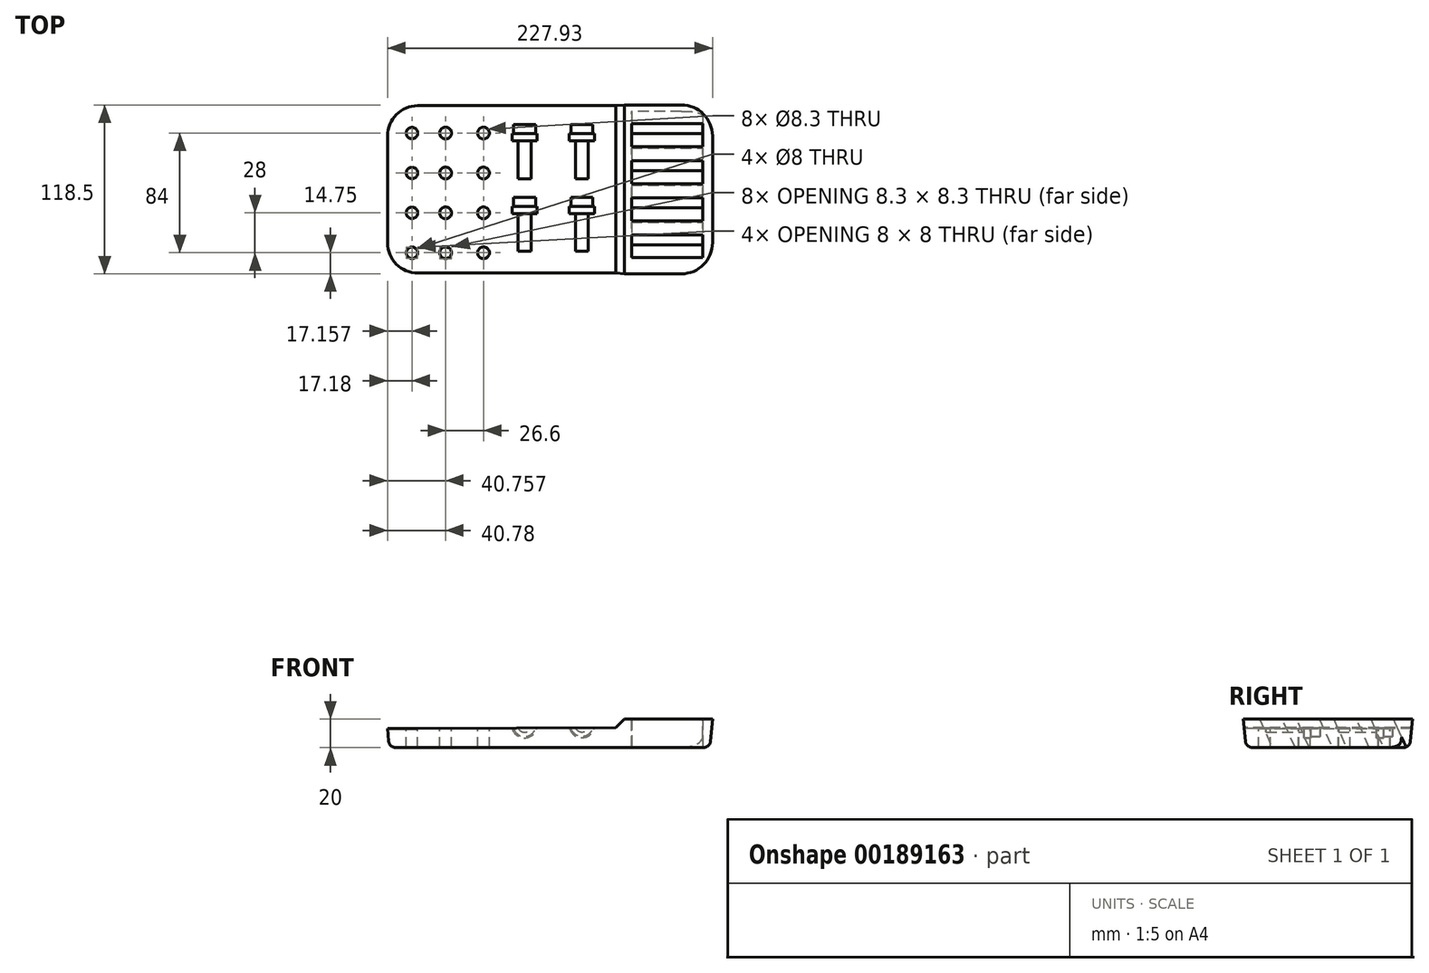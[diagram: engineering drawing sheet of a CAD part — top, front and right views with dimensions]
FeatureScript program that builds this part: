
annotation { "Feature Type Name" : "Feature", "Feature Type Description" : "" }
export const myFeature = defineFeature(function(context is Context, id is Id, definition is map)
    precondition{}
    {
        {
            var Q0;
            Q0=qCreatedBy(makeId("Top.planeOp"),FACE);
            var sketch = newSketch(context, id + "F0", { "sketchPlane" : qUnion([Q0])});
            skLineSegment(sketch, "E0.bottom", {"start": v(20, 0) * mm, "end": v(205, 0) * mm});
            skLineSegment(sketch, "E0.top", {"start": v(20, 115) * mm, "end": v(205, 115) * mm});
            skLineSegment(sketch, "E0.left", {"start": v(0, 20) * mm, "end": v(0, 95) * mm});
            skLineSegment(sketch, "E0.right", {"start": v(225, 20) * mm, "end": v(225, 95) * mm});
            skPoint(sketch, "E1.visualSharp", {"position": v(0, 115) * mm});
            skArc(sketch, "E1.filletArc", {"start": v(20, 115) * mm, "mid": v(5.86, 109.14) * mm, "end": v(0, 95) * mm});
            skPoint(sketch, "E2.visualSharp", {"position": v(225, 115) * mm});
            skArc(sketch, "E2.filletArc", {"start": v(225, 95) * mm, "mid": v(219.14, 109.14) * mm, "end": v(205, 115) * mm});
            skPoint(sketch, "E3.visualSharp", {"position": v(0, 0) * mm});
            skArc(sketch, "E3.filletArc", {"start": v(0, 20) * mm, "mid": v(5.86, 5.86) * mm, "end": v(20, 0) * mm});
            skPoint(sketch, "E4.visualSharp", {"position": v(225, 0) * mm});
            skArc(sketch, "E4.filletArc", {"start": v(205, 0) * mm, "mid": v(219.14, 5.86) * mm, "end": v(225, 20) * mm});
            skSolve(sketch);
        }
        {
            var Q0;
            Q0=makeQuery(id+"F0.imprint","IMPRINT",FACE,{"disambiguationData":[TD([[makeQuery(id+"F0.imprint","IMPRINT",EDGE,{"derivedFrom":sQuery(id+"F0.wireOp",EDGE,"E0.bottom")}),1.0]])]});
            extrude(context, id + "F1", {"entities" : qUnion([Q0]), "depth" : 20 * mm, "hasDraft" : true, "draftAngle" : 5 * degree});
        }
        {
            var Q0;
            Q0=makeQuery(id+"F1.opExtrude","CAP_FACE",FACE,{"disambiguationData":[OSD([sQuery(id+"F0.wireOp",EDGE,"E0.bottom"),sQuery(id+"F0.wireOp",EDGE,"E0.top"),sQuery(id+"F0.wireOp",EDGE,"E0.left"),sQuery(id+"F0.wireOp",EDGE,"E0.right"),sQuery(id+"F0.wireOp",EDGE,"E1.filletArc"),sQuery(id+"F0.wireOp",EDGE,"E2.filletArc"),sQuery(id+"F0.wireOp",EDGE,"E3.filletArc"),sQuery(id+"F0.wireOp",EDGE,"E4.filletArc")])],"isStart":true});
            fillet(context, id + "F2", {"entities" : qUnion([Q0]), "radius" : 5 * mm, "tangentPropagation" : true, "allowEdgeOverflow" : false});
        }
        {
            var Q0;
            Q0=qCreatedBy(makeId("Right.planeOp"),FACE);
            cPlane(context, id + "F3", {"entities" : qUnion([Q0]), "cplaneType" : CPlaneType.OFFSET, "offset" : 220 * mm, "width" : 150 * mm, "height" : 150 * mm});
        }
        {
            var Q0;
            Q0=qCreatedBy(id+"F3.planeOp",FACE);
            var sketch = newSketch(context, id + "F4", { "sketchPlane" : qUnion([Q0])});
            skLineSegment(sketch, "E5", {"start": v(0, 0) * mm, "end": v(112.5, 0) * mm, "construction": true});
            skLineSegment(sketch, "E6", {"start": v(112.5, 0) * mm, "end": v(96.5, 0) * mm});
            skLineSegment(sketch, "E7", {"start": v(112.5, 0) * mm, "end": v(112.5, 20) * mm, "construction": true});
            skLineSegment(sketch, "E8", {"start": v(112.5, 20) * mm, "end": v(103.5, 20) * mm, "construction": true});
            skLineSegment(sketch, "E9", {"start": v(112.5, 0) * mm, "end": v(103.5, 20) * mm});
            skLineSegment(sketch, "E10", {"start": v(103.5, 20) * mm, "end": v(87.5, 20) * mm});
            skLineSegment(sketch, "E11", {"start": v(87.5, 20) * mm, "end": v(96.5, 0) * mm});
            skLineSegment(sketch, "E12", {"start": v(96.5, 0) * mm, "end": v(86.5, 0) * mm, "construction": true});
            skLineSegment(sketch, "E13", {"start": v(86.5, 0) * mm, "end": v(70.5, 0) * mm, "construction": true});
            skLineSegment(sketch, "E14", {"start": v(70.5, 0) * mm, "end": v(60.5, 0) * mm, "construction": true});
            skLineSegment(sketch, "E15", {"start": v(60.5, 0) * mm, "end": v(44.5, 0) * mm, "construction": true});
            skLineSegment(sketch, "E16", {"start": v(44.5, 0) * mm, "end": v(34.5, 0) * mm, "construction": true});
            skLineSegment(sketch, "E17", {"start": v(34.5, 0) * mm, "end": v(18.5, 0) * mm, "construction": true});
            skLineSegment(sketch, "E18", {"start": v(87.5, 20) * mm, "end": v(77.5, 20) * mm, "construction": true});
            skLineSegment(sketch, "E19", {"start": v(77.5, 20) * mm, "end": v(61.5, 20) * mm, "construction": true});
            skLineSegment(sketch, "E20", {"start": v(61.5, 20) * mm, "end": v(51.5, 20) * mm, "construction": true});
            skLineSegment(sketch, "E21", {"start": v(51.5, 20) * mm, "end": v(35.5, 20) * mm, "construction": true});
            skLineSegment(sketch, "E22", {"start": v(35.5, 20) * mm, "end": v(25.5, 20) * mm, "construction": true});
            skLineSegment(sketch, "E23", {"start": v(25.5, 20) * mm, "end": v(9.5, 20) * mm, "construction": true});
            skLineSegment(sketch, "E24", {"start": v(86.5, 0) * mm, "end": v(77.5, 20) * mm});
            skLineSegment(sketch, "E25", {"start": v(61.5, 20) * mm, "end": v(70.5, 0) * mm});
            skLineSegment(sketch, "E26", {"start": v(77.5, 20) * mm, "end": v(61.5, 20) * mm});
            skLineSegment(sketch, "E27", {"start": v(70.5, 0) * mm, "end": v(86.5, 0) * mm});
            skLineSegment(sketch, "E28", {"start": v(60.5, 0) * mm, "end": v(44.5, 0) * mm});
            skLineSegment(sketch, "E29", {"start": v(44.5, 0) * mm, "end": v(35.5, 20) * mm});
            skLineSegment(sketch, "E30", {"start": v(35.5, 20) * mm, "end": v(51.5, 20) * mm});
            skLineSegment(sketch, "E31", {"start": v(51.5, 20) * mm, "end": v(60.5, 0) * mm});
            skLineSegment(sketch, "E32", {"start": v(25.5, 20) * mm, "end": v(9.5, 20) * mm});
            skLineSegment(sketch, "E33", {"start": v(9.5, 20) * mm, "end": v(18.5, 0) * mm});
            skLineSegment(sketch, "E34", {"start": v(18.5, 0) * mm, "end": v(34.5, 0) * mm});
            skLineSegment(sketch, "E35", {"start": v(34.5, 0) * mm, "end": v(25.5, 20) * mm});
            skSolve(sketch);
        }
        {
            var Q0;
            Q0 = qSketchRegion(id + "F4", true);
            extrude(context, id + "F5", {"entities" : qUnion([Q0]), "operationType" : NewBodyOperationType.REMOVE, "oppositeDirection" : true, "depth" : 50 * mm});
        }
        {
            var Q0;
            Q0=qCreatedBy(makeId("Front.planeOp"),FACE);
            var sketch = newSketch(context, id + "F6", { "sketchPlane" : qUnion([Q0])});
            skLineSegment(sketch, "E36", {"start": v(0, 0) * mm, "end": v(165, 0) * mm, "construction": true});
            skLineSegment(sketch, "E37", {"start": v(165, 0) * mm, "end": v(165, 20) * mm, "construction": true});
            skLineSegment(sketch, "E38", {"start": v(165, 20) * mm, "end": v(165, 16) * mm, "construction": true});
            skPoint(sketch, "E38.endSnap0", {"position": v(165, 10) * mm});
            skLineSegment(sketch, "E39", {"start": v(165, 20) * mm, "end": v(160.99, 15.99) * mm});
            skLineSegment(sketch, "E40", {"start": v(160.99, 15.99) * mm, "end": v(-6.74, 15.45) * mm});
            skPoint(sketch, "E40.endSnap0", {"position": v(160.45, 15.45) * mm});
            skPoint(sketch, "E41.orphan", {"position": v(155.9, 10.9) * mm});
            skLineSegment(sketch, "E42", {"start": v(-6.74, 15.45) * mm, "end": v(-6.76, 20) * mm});
            skLineSegment(sketch, "E43", {"start": v(165, 20) * mm, "end": v(-6.76, 20) * mm});
            skSolve(sketch);
        }
        {
            var Q0;
            Q0 = qSketchRegion(id + "F6", true);
            extrude(context, id + "F7", {"entities" : qUnion([Q0]), "operationType" : NewBodyOperationType.REMOVE, "endBound" : BoundingType.SYMMETRIC, "oppositeDirection" : true, "depth" : 240 * mm});
        }
        {
            var Q0;
            Q0=makeQuery(id+"F7.boolean.opBoolean","COPY",FACE,{"derivedFrom":makeQuery(id+"F7.opExtrude","SWEPT_FACE",FACE,{"disambiguationData":[OSD([sQuery(id+"F6.wireOp",EDGE,"E40")])]})});
            var sketch = newSketch(context, id + "F8", { "sketchPlane" : qUnion([Q0])});
            skLineSegment(sketch, "E44.bottom", {"start": v(0, 0) * mm, "end": v(16, 0) * mm, "construction": true});
            skLineSegment(sketch, "E44.top", {"start": v(0, 13) * mm, "end": v(16, 13) * mm, "construction": true});
            skLineSegment(sketch, "E44.left", {"start": v(0, 0) * mm, "end": v(0, 13) * mm, "construction": true});
            skLineSegment(sketch, "E44.right", {"start": v(16, 0) * mm, "end": v(16, 13) * mm, "construction": true});
            skLineSegment(sketch, "E45.bottom", {"start": v(16, 13) * mm, "end": v(39.6, 13) * mm, "construction": true});
            skLineSegment(sketch, "E45.top", {"start": v(16, 41) * mm, "end": v(39.6, 41) * mm, "construction": true});
            skLineSegment(sketch, "E45.left", {"start": v(16, 13) * mm, "end": v(16, 41) * mm, "construction": true});
            skLineSegment(sketch, "E45.right", {"start": v(39.6, 13) * mm, "end": v(39.6, 41) * mm, "construction": true});
            skLineSegment(sketch, "E46.top", {"start": v(16, 69) * mm, "end": v(39.6, 69) * mm, "construction": true});
            skLineSegment(sketch, "E46.left", {"start": v(16, 41) * mm, "end": v(16, 69) * mm, "construction": true});
            skLineSegment(sketch, "E46.right", {"start": v(39.6, 41) * mm, "end": v(39.6, 69) * mm, "construction": true});
            skLineSegment(sketch, "E47.top", {"start": v(16, 97) * mm, "end": v(39.6, 97) * mm, "construction": true});
            skLineSegment(sketch, "E47.left", {"start": v(16, 69) * mm, "end": v(16, 97) * mm, "construction": true});
            skLineSegment(sketch, "E47.right", {"start": v(39.6, 69) * mm, "end": v(39.6, 97) * mm, "construction": true});
            skLineSegment(sketch, "E48.bottom", {"start": v(39.6, 13) * mm, "end": v(66.2, 13) * mm, "construction": true});
            skLineSegment(sketch, "E48.top", {"start": v(39.6, 41) * mm, "end": v(66.2, 41) * mm, "construction": true});
            skLineSegment(sketch, "E48.right", {"start": v(66.2, 13) * mm, "end": v(66.2, 41) * mm, "construction": true});
            skLineSegment(sketch, "E49.top", {"start": v(39.6, 69) * mm, "end": v(66.2, 69) * mm, "construction": true});
            skLineSegment(sketch, "E49.right", {"start": v(66.2, 41) * mm, "end": v(66.2, 69) * mm, "construction": true});
            skLineSegment(sketch, "E50.top", {"start": v(39.6, 97) * mm, "end": v(66.2, 97) * mm, "construction": true});
            skLineSegment(sketch, "E50.right", {"start": v(66.2, 69) * mm, "end": v(66.2, 97) * mm, "construction": true});
            skCircle(sketch, "E51", {"center": v(16, 13) * mm, "radius": 4 * mm});
            skCircle(sketch, "E52", {"center": v(16, 41) * mm, "radius": 4 * mm});
            skCircle(sketch, "E53", {"center": v(16, 69) * mm, "radius": 4 * mm});
            skCircle(sketch, "E54", {"center": v(16, 97) * mm, "radius": 4 * mm});
            skCircle(sketch, "E55", {"center": v(39.6, 97) * mm, "radius": 4.15 * mm});
            skCircle(sketch, "E56", {"center": v(39.6, 69) * mm, "radius": 4.15 * mm});
            skCircle(sketch, "E57", {"center": v(39.6, 41) * mm, "radius": 4.15 * mm});
            skCircle(sketch, "E58", {"center": v(39.6, 13) * mm, "radius": 4.15 * mm});
            skCircle(sketch, "E59", {"center": v(66.2, 13) * mm, "radius": 4.15 * mm});
            skCircle(sketch, "E60", {"center": v(66.2, 41) * mm, "radius": 4.15 * mm});
            skCircle(sketch, "E61", {"center": v(66.2, 69) * mm, "radius": 4.15 * mm});
            skCircle(sketch, "E62", {"center": v(66.2, 97) * mm, "radius": 4.15 * mm});
            skSolve(sketch);
        }
        {
            var Q0;
            Q0 = qSketchRegion(id + "F8", true);
            extrude(context, id + "F9", {"entities" : qUnion([Q0]), "operationType" : NewBodyOperationType.REMOVE, "endBound" : BoundingType.THROUGH_ALL, "oppositeDirection" : true, "depth" : 25 * mm});
        }
        {
            var Q0;
            Q0=makeQuery(id+"F7.boolean.opBoolean","COPY",FACE,{"derivedFrom":makeQuery(id+"F7.opExtrude","SWEPT_FACE",FACE,{"disambiguationData":[OSD([sQuery(id+"F6.wireOp",EDGE,"E40")])]})});
            var sketch = newSketch(context, id + "F10", { "sketchPlane" : qUnion([Q0])});
            skLineSegment(sketch, "E63.bottom", {"start": v(0, 0) * mm, "end": v(95, 0) * mm, "construction": true});
            skLineSegment(sketch, "E63.top", {"start": v(0, 14) * mm, "end": v(95, 14) * mm, "construction": true});
            skLineSegment(sketch, "E63.left", {"start": v(0, 0) * mm, "end": v(0, 14) * mm, "construction": true});
            skLineSegment(sketch, "E63.right", {"start": v(95, 0) * mm, "end": v(95, 14) * mm, "construction": true});
            skLineSegment(sketch, "E64.bottom", {"start": v(95, 14) * mm, "end": v(100, 14) * mm});
            skLineSegment(sketch, "E64.left", {"start": v(95, 14) * mm, "end": v(95, 40.5) * mm});
            skLineSegment(sketch, "E64.right", {"start": v(100, 14) * mm, "end": v(100, 40.5) * mm});
            skLineSegment(sketch, "E65.bottom", {"start": v(100, 40.5) * mm, "end": v(104, 40.5) * mm});
            skLineSegment(sketch, "E65.top", {"start": v(103, 45.5) * mm, "end": v(104, 45.5) * mm});
            skLineSegment(sketch, "E65.left", {"start": v(95, 40.5) * mm, "end": v(95, 45.5) * mm});
            skLineSegment(sketch, "E65.right", {"start": v(104, 40.5) * mm, "end": v(104, 45.5) * mm});
            skLineSegment(sketch, "E66.top", {"start": v(95, 52) * mm, "end": v(103, 52) * mm});
            skLineSegment(sketch, "E66.left", {"start": v(95, 45.5) * mm, "end": v(95, 52) * mm});
            skLineSegment(sketch, "E66.right", {"start": v(103, 45.5) * mm, "end": v(103, 52) * mm});
            skSolve(sketch);
        }
        {
            var Q0;
            Q0=makeQuery(id+"F10.imprint","IMPRINT",FACE,{"disambiguationData":[TD([[makeQuery(id+"F10.imprint","IMPRINT",EDGE,{"derivedFrom":sQuery(id+"F10.wireOp",EDGE,"E64.bottom")}),1.0]])]});
            var Q1;
            Q1=sQuery(id+"F10.wireOp",EDGE,"E64.left");
            revolve(context, id + "F11", {"operationType" : NewBodyOperationType.REMOVE, "entities" : qUnion([Q0]), "axis" : qUnion([Q1]), "revolveType" : RevolveType.FULL, "oppositeDirection" : true});
        }
        {
            var Q0;
            Q0=makeQuery(id+"F7.boolean.opBoolean","COPY",FACE,{"derivedFrom":makeQuery(id+"F7.opExtrude","SWEPT_FACE",FACE,{"disambiguationData":[OSD([sQuery(id+"F6.wireOp",EDGE,"E40")])]})});
            var sketch = newSketch(context, id + "F12", { "sketchPlane" : qUnion([Q0])});
            skLineSegment(sketch, "E67.bottom", {"start": v(0, 0) * mm, "end": v(135.2, 0) * mm, "construction": true});
            skLineSegment(sketch, "E67.top", {"start": v(0, 14) * mm, "end": v(135.2, 14) * mm, "construction": true});
            skLineSegment(sketch, "E67.left", {"start": v(0, 0) * mm, "end": v(0, 14) * mm, "construction": true});
            skLineSegment(sketch, "E67.right", {"start": v(135.2, 0) * mm, "end": v(135.2, 14) * mm, "construction": true});
            skLineSegment(sketch, "E68.bottom", {"start": v(135.2, 14) * mm, "end": v(140.2, 14) * mm});
            skLineSegment(sketch, "E68.left", {"start": v(135.2, 14) * mm, "end": v(135.2, 40.5) * mm});
            skLineSegment(sketch, "E68.right", {"start": v(140.2, 14) * mm, "end": v(140.2, 40.5) * mm});
            skLineSegment(sketch, "E69.bottom", {"start": v(140.2, 40.5) * mm, "end": v(144.2, 40.5) * mm});
            skLineSegment(sketch, "E69.top", {"start": v(143.2, 45.5) * mm, "end": v(144.2, 45.5) * mm});
            skLineSegment(sketch, "E69.left", {"start": v(135.2, 40.5) * mm, "end": v(135.2, 45.5) * mm});
            skLineSegment(sketch, "E69.right", {"start": v(144.2, 40.5) * mm, "end": v(144.2, 45.5) * mm});
            skLineSegment(sketch, "E70.top", {"start": v(135.2, 52) * mm, "end": v(143.2, 52) * mm});
            skLineSegment(sketch, "E70.left", {"start": v(135.2, 45.5) * mm, "end": v(135.2, 52) * mm});
            skLineSegment(sketch, "E70.right", {"start": v(143.2, 45.5) * mm, "end": v(143.2, 52) * mm});
            skSolve(sketch);
        }
        {
            var Q0;
            Q0=makeQuery(id+"F12.imprint","IMPRINT",FACE,{"disambiguationData":[TD([[makeQuery(id+"F12.imprint","IMPRINT",EDGE,{"derivedFrom":sQuery(id+"F12.wireOp",EDGE,"E68.bottom")}),1.0]])]});
            var Q1;
            Q1=sQuery(id+"F12.wireOp",EDGE,"E68.left");
            revolve(context, id + "F13", {"operationType" : NewBodyOperationType.REMOVE, "entities" : qUnion([Q0]), "axis" : qUnion([Q1]), "revolveType" : RevolveType.FULL, "oppositeDirection" : true});
        }
        {
            var Q0;
            Q0=makeQuery(id+"F7.boolean.opBoolean","COPY",FACE,{"derivedFrom":makeQuery(id+"F7.opExtrude","SWEPT_FACE",FACE,{"disambiguationData":[OSD([sQuery(id+"F6.wireOp",EDGE,"E40")])]})});
            var sketch = newSketch(context, id + "F14", { "sketchPlane" : qUnion([Q0])});
            skLineSegment(sketch, "E71.bottom", {"start": v(0, 0) * mm, "end": v(95, 0) * mm, "construction": true});
            skLineSegment(sketch, "E71.top", {"start": v(0, 65) * mm, "end": v(95, 65) * mm, "construction": true});
            skLineSegment(sketch, "E71.left", {"start": v(0, 0) * mm, "end": v(0, 65) * mm, "construction": true});
            skLineSegment(sketch, "E71.right", {"start": v(95, 0) * mm, "end": v(95, 65) * mm, "construction": true});
            skLineSegment(sketch, "E72.bottom", {"start": v(95, 65) * mm, "end": v(100, 65) * mm});
            skLineSegment(sketch, "E72.left", {"start": v(95, 65) * mm, "end": v(95, 91.5) * mm});
            skLineSegment(sketch, "E72.right", {"start": v(100, 65) * mm, "end": v(100, 91.5) * mm});
            skLineSegment(sketch, "E73.bottom", {"start": v(100, 91.5) * mm, "end": v(104, 91.5) * mm});
            skLineSegment(sketch, "E73.top", {"start": v(103, 96.5) * mm, "end": v(104, 96.5) * mm});
            skLineSegment(sketch, "E73.left", {"start": v(95, 91.5) * mm, "end": v(95, 96.5) * mm});
            skLineSegment(sketch, "E73.right", {"start": v(104, 91.5) * mm, "end": v(104, 96.5) * mm});
            skLineSegment(sketch, "E74.top", {"start": v(95, 103) * mm, "end": v(103, 103) * mm});
            skLineSegment(sketch, "E74.left", {"start": v(95, 96.5) * mm, "end": v(95, 103) * mm});
            skLineSegment(sketch, "E74.right", {"start": v(103, 96.5) * mm, "end": v(103, 103) * mm});
            skSolve(sketch);
        }
        {
            var Q0;
            Q0=makeQuery(id+"F14.imprint","IMPRINT",FACE,{"disambiguationData":[TD([[makeQuery(id+"F14.imprint","IMPRINT",EDGE,{"derivedFrom":sQuery(id+"F14.wireOp",EDGE,"E72.bottom")}),1.0]])]});
            var Q1;
            Q1=sQuery(id+"F14.wireOp",EDGE,"E72.left");
            revolve(context, id + "F15", {"operationType" : NewBodyOperationType.REMOVE, "entities" : qUnion([Q0]), "axis" : qUnion([Q1]), "revolveType" : RevolveType.FULL, "oppositeDirection" : true});
        }
        {
            var Q0;
            Q0=makeQuery(id+"F7.boolean.opBoolean","COPY",FACE,{"derivedFrom":makeQuery(id+"F7.opExtrude","SWEPT_FACE",FACE,{"disambiguationData":[OSD([sQuery(id+"F6.wireOp",EDGE,"E40")])]})});
            var sketch = newSketch(context, id + "F16", { "sketchPlane" : qUnion([Q0])});
            skLineSegment(sketch, "E75.bottom", {"start": v(0, 0) * mm, "end": v(135.2, 0) * mm, "construction": true});
            skLineSegment(sketch, "E75.top", {"start": v(0, 65) * mm, "end": v(135.2, 65) * mm, "construction": true});
            skLineSegment(sketch, "E75.left", {"start": v(0, 0) * mm, "end": v(0, 65) * mm, "construction": true});
            skLineSegment(sketch, "E75.right", {"start": v(135.2, 0) * mm, "end": v(135.2, 65) * mm, "construction": true});
            skLineSegment(sketch, "E76.bottom", {"start": v(135.2, 65) * mm, "end": v(140.2, 65) * mm});
            skLineSegment(sketch, "E76.left", {"start": v(135.2, 65) * mm, "end": v(135.2, 91.5) * mm});
            skLineSegment(sketch, "E76.right", {"start": v(140.2, 65) * mm, "end": v(140.2, 91.5) * mm});
            skLineSegment(sketch, "E77.bottom", {"start": v(140.2, 91.5) * mm, "end": v(144.2, 91.5) * mm});
            skLineSegment(sketch, "E77.top", {"start": v(143.2, 96.5) * mm, "end": v(144.2, 96.5) * mm});
            skLineSegment(sketch, "E77.left", {"start": v(135.2, 91.5) * mm, "end": v(135.2, 96.5) * mm});
            skLineSegment(sketch, "E77.right", {"start": v(144.2, 91.5) * mm, "end": v(144.2, 96.5) * mm});
            skLineSegment(sketch, "E78.top", {"start": v(135.2, 103) * mm, "end": v(143.2, 103) * mm});
            skLineSegment(sketch, "E78.left", {"start": v(135.2, 96.5) * mm, "end": v(135.2, 103) * mm});
            skLineSegment(sketch, "E78.right", {"start": v(143.2, 96.5) * mm, "end": v(143.2, 103) * mm});
            skSolve(sketch);
        }
        {
            var Q0;
            Q0=makeQuery(id+"F16.imprint","IMPRINT",FACE,{"disambiguationData":[TD([[makeQuery(id+"F16.imprint","IMPRINT",EDGE,{"derivedFrom":sQuery(id+"F16.wireOp",EDGE,"E76.bottom")}),1.0]])]});
            var Q1;
            Q1=sQuery(id+"F16.wireOp",EDGE,"E76.left");
            revolve(context, id + "F17", {"operationType" : NewBodyOperationType.REMOVE, "entities" : qUnion([Q0]), "axis" : qUnion([Q1]), "revolveType" : RevolveType.FULL, "oppositeDirection" : true});
        }
        {
            var Q0;
            Q0=qCreatedBy(makeId("Front.planeOp"),FACE);
            var sketch = newSketch(context, id + "F18", { "sketchPlane" : qUnion([Q0])});
            skLineSegment(sketch, "E79.0.1", {"start": v(20, 15.54) * mm, "end": v(160.99, 15.99) * mm});
            skLineSegment(sketch, "E79.0.2", {"start": v(20, 15.54) * mm, "end": v(20, 13.54) * mm});
            skLineSegment(sketch, "E80", {"start": v(160.99, 15.99) * mm, "end": v(158.9, 13.9) * mm});
            skLineSegment(sketch, "E81", {"start": v(20, 15.54) * mm, "end": v(20, 13.54) * mm, "construction": true});
            skLineSegment(sketch, "E82", {"start": v(20, 13.54) * mm, "end": v(-9.15, 13.54) * mm});
            skLineSegment(sketch, "E83", {"start": v(-9.15, 13.54) * mm, "end": v(-9.15, 15.54) * mm});
            skLineSegment(sketch, "E84", {"start": v(-9.15, 15.54) * mm, "end": v(160.99, 15.99) * mm});
            skLineSegment(sketch, "E85", {"start": v(20, 13.54) * mm, "end": v(158.9, 13.9) * mm});
            skPoint(sketch, "E79.0.3.start.orphan", {"position": v(20, 4.56) * mm});
            skPoint(sketch, "E79.0.4.end.orphan", {"position": v(205, 4.56) * mm});
            skPoint(sketch, "E79.0.4.start.orphan", {"position": v(205, 20) * mm});
            skPoint(sketch, "E79.0.0.end.orphan", {"position": v(165, 20) * mm});
            skSolve(sketch);
        }
        {
            var Q0;
            Q0 = qSketchRegion(id + "F18", true);
            extrude(context, id + "F19", {"entities" : qUnion([Q0]), "operationType" : NewBodyOperationType.REMOVE, "endBound" : BoundingType.SYMMETRIC, "oppositeDirection" : true, "depth" : 250 * mm});
        }
    });
